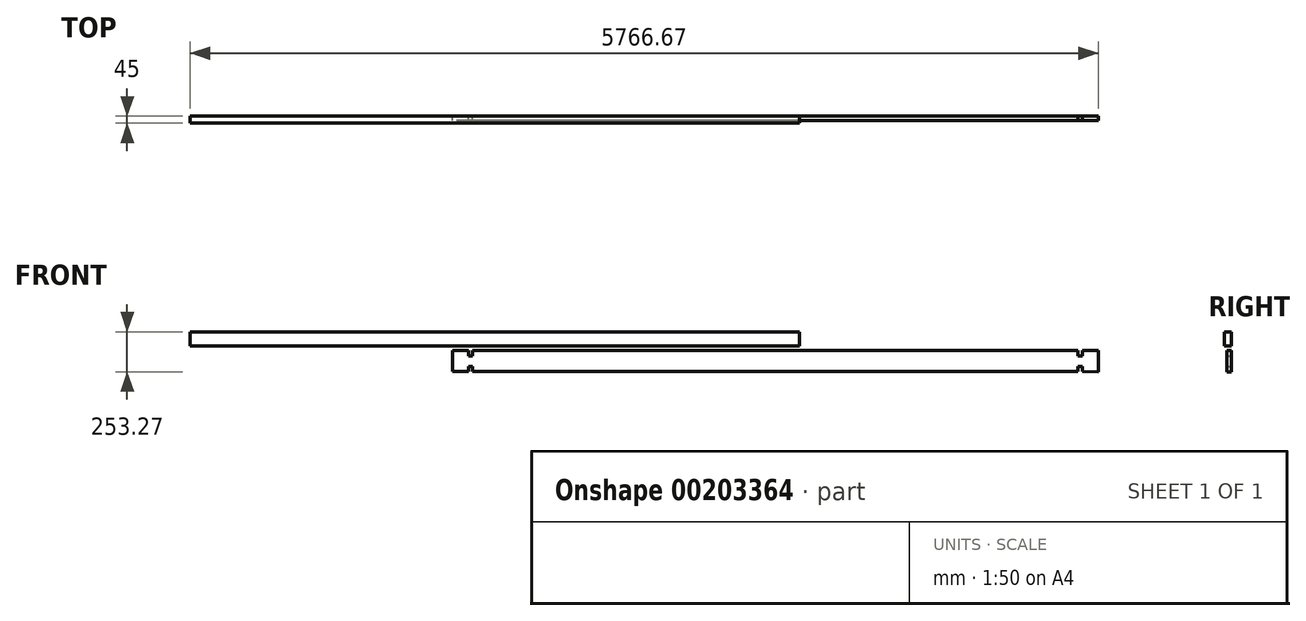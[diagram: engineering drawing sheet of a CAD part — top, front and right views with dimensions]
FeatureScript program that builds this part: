
annotation { "Feature Type Name" : "Feature", "Feature Type Description" : "" }
export const myFeature = defineFeature(function(context is Context, id is Id, definition is map)
    precondition{}
    {
        {
            var Q0;
            Q0=qCreatedBy(makeId("Front.planeOp"),FACE);
            var sketch = newSketch(context, id + "F0", { "sketchPlane" : qUnion([Q0])});
            skLineSegment(sketch, "E0.bottom", {"start": v(1922, 67.5) * mm, "end": v(-1922, 67.5) * mm});
            skLineSegment(sketch, "E0.top", {"start": v(1922, -67.5) * mm, "end": v(-1922, -67.5) * mm});
            skLineSegment(sketch, "E0.left", {"start": v(1922, 67.5) * mm, "end": v(1922, 33.75) * mm});
            skLineSegment(sketch, "E0.right", {"start": v(-1922, 67.5) * mm, "end": v(-1922, 33.75) * mm});
            skPoint(sketch, "E0.middle", {"position": v(0, 0) * mm});
            skLineSegment(sketch, "E1", {"start": v(-1922, -33.75) * mm, "end": v(-1922, -67.5) * mm});
            skLineSegment(sketch, "E2", {"start": v(-1922, 33.75) * mm, "end": v(-1950, 33.75) * mm});
            skLineSegment(sketch, "E3", {"start": v(-1922, -33.75) * mm, "end": v(-1950, -33.75) * mm});
            skLineSegment(sketch, "E4", {"start": v(-1950, 33.75) * mm, "end": v(-1950, 67.5) * mm});
            skLineSegment(sketch, "E5", {"start": v(-1950, -33.75) * mm, "end": v(-1950, -67.5) * mm});
            skLineSegment(sketch, "E6", {"start": v(-1950, -67.5) * mm, "end": v(-2050, -67.5) * mm});
            skLineSegment(sketch, "E7", {"start": v(-2050, -67.5) * mm, "end": v(-2050, 67.5) * mm});
            skLineSegment(sketch, "E8", {"start": v(-2050, 67.5) * mm, "end": v(-1950, 67.5) * mm});
            skLineSegment(sketch, "E9", {"start": v(1922, -33.75) * mm, "end": v(1922, -67.5) * mm});
            skLineSegment(sketch, "E10", {"start": v(1922, 33.75) * mm, "end": v(1950, 33.75) * mm});
            skLineSegment(sketch, "E11", {"start": v(1922, -33.75) * mm, "end": v(1950, -33.75) * mm});
            skLineSegment(sketch, "E12", {"start": v(1950, -33.75) * mm, "end": v(1950, -67.25) * mm});
            skLineSegment(sketch, "E13", {"start": v(1950, 33.75) * mm, "end": v(1950, 67.25) * mm});
            skLineSegment(sketch, "E14", {"start": v(1950, 67.25) * mm, "end": v(2050, 67.25) * mm});
            skLineSegment(sketch, "E15", {"start": v(2050, 67.25) * mm, "end": v(2050, -67.75) * mm});
            skLineSegment(sketch, "E16", {"start": v(2050, -67.75) * mm, "end": v(1950, -67.25) * mm});
            skSolve(sketch);
        }
        {
            var Q0;
            Q0 = qSketchRegion(id + "F0", true);
            extrude(context, id + "F1", {"entities" : qUnion([Q0]), "depth" : 28 * mm});
        }
        {
            var Q0;
            Q0=qCreatedBy(makeId("Front.planeOp"),FACE);
            var sketch = newSketch(context, id + "F2", { "sketchPlane" : qUnion([Q0])});
            skLineSegment(sketch, "E17.bottom", {"start": v(-3716.67, 185.52) * mm, "end": v(153.33, 185.52) * mm});
            skLineSegment(sketch, "E17.top", {"start": v(-3716.67, 95.52) * mm, "end": v(153.33, 95.52) * mm});
            skLineSegment(sketch, "E17.left", {"start": v(-3716.67, 185.52) * mm, "end": v(-3716.67, 95.52) * mm});
            skLineSegment(sketch, "E17.right", {"start": v(153.33, 185.52) * mm, "end": v(153.33, 95.52) * mm});
            skSolve(sketch);
        }
        {
            var Q0;
            Q0 = qSketchRegion(id + "F2", true);
            extrude(context, id + "F3", {"entities" : qUnion([Q0]), "depth" : 45 * mm});
        }
    });
